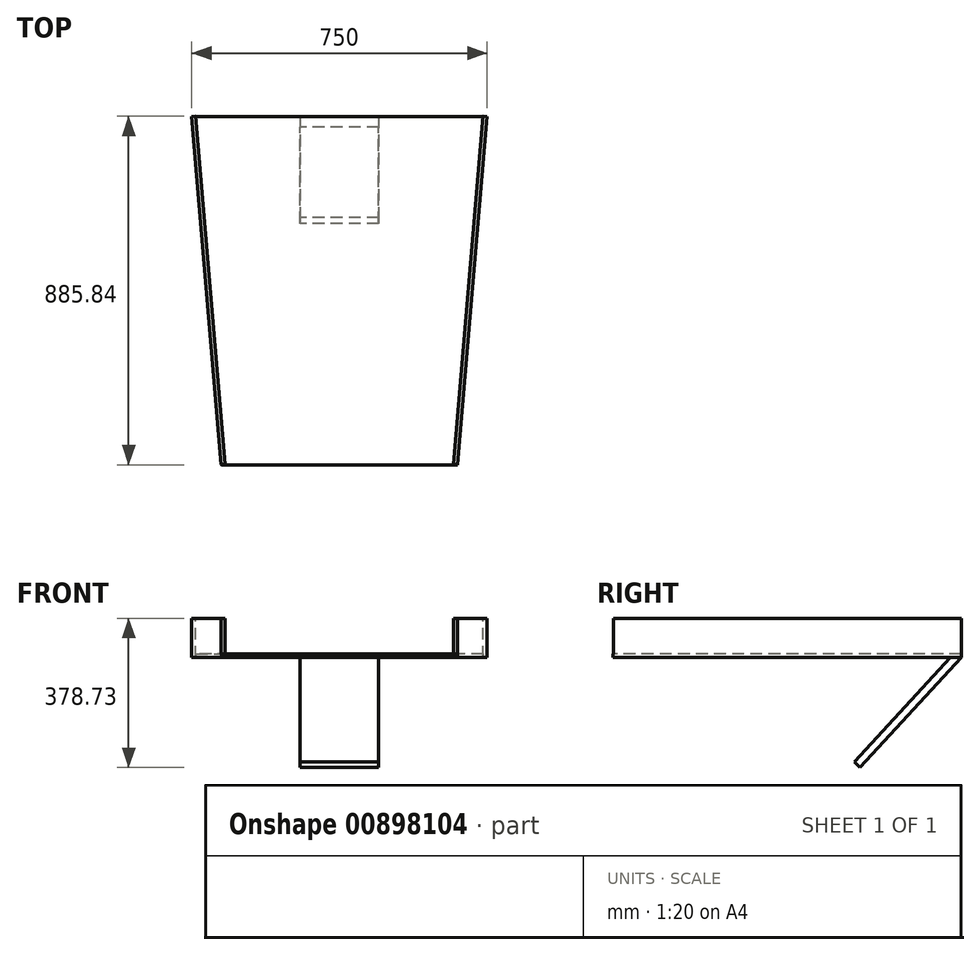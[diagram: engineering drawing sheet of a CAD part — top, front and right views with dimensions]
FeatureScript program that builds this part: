
annotation { "Feature Type Name" : "Feature", "Feature Type Description" : "" }
export const myFeature = defineFeature(function(context is Context, id is Id, definition is map)
    precondition{}
    {
        {
            var Q0;
            Q0=qCreatedBy(makeId("Top.planeOp"),FACE);
            var sketch = newSketch(context, id + "F0", { "sketchPlane" : qUnion([Q0])});
            skLineSegment(sketch, "E0.bottom", {"start": v(300, -442.5) * mm, "end": v(-300, -442.5) * mm});
            skLineSegment(sketch, "E0.top", {"start": v(375, 442.5) * mm, "end": v(-375, 442.5) * mm});
            skPoint(sketch, "E0.middle", {"position": v(0, 0) * mm});
            skLineSegment(sketch, "E1.bottom", {"start": v(-300, 442.5) * mm, "end": v(300, 442.5) * mm});
            skLineSegment(sketch, "E1.top", {"start": v(-300, -442.5) * mm, "end": v(300, -442.5) * mm});
            skLineSegment(sketch, "E2", {"start": v(-375, 442.5) * mm, "end": v(-300, -442.5) * mm});
            skLineSegment(sketch, "E3", {"start": v(300, -442.5) * mm, "end": v(375, 442.5) * mm});
            skPoint(sketch, "E4.orphan", {"position": v(-375, -442.5) * mm});
            skPoint(sketch, "E0.left.start.orphan", {"position": v(375, -442.5) * mm});
            skSolve(sketch);
        }
        {
            var Q0;
            {var subQ0=sQuery(id+"F0.wireOp",EDGE,"E1.bottom");Q0=makeQuery(id+"F0.imprint","IMPRINT",FACE,{"disambiguationData":[TD([[makeQuery(id+"F0.imprint","IMPRINT",EDGE,{"derivedFrom":subQ0}),-1.0]])]});}
            var Q1;
            Q1 = qSketchRegion(id + "F0", true);
            extrude(context, id + "F1", {"entities" : qUnion([Q0, Q1]), "depth" : 10 * mm, "offsetDistance" : 25 * mm});
        }
        {
            var Q0;
            Q0=makeQuery(id+"F1.opExtrude","SWEPT_FACE",FACE,{"disambiguationData":[OSD([sQuery(id+"F0.wireOp",EDGE,"E2")])]});
            var sketch = newSketch(context, id + "F2", { "sketchPlane" : qUnion([Q0])});
            skLineSegment(sketch, "E5.bottom", {"start": v(-472.59, 0) * mm, "end": v(414.67, 0) * mm});
            skLineSegment(sketch, "E5.top", {"start": v(-472.59, 100) * mm, "end": v(414.67, 100) * mm});
            skLineSegment(sketch, "E5.left", {"start": v(-472.59, 0) * mm, "end": v(-472.59, 100) * mm});
            skLineSegment(sketch, "E5.right", {"start": v(414.67, 0) * mm, "end": v(414.67, 100) * mm});
            skSolve(sketch);
        }
        {
            var Q0;
            Q0 = qSketchRegion(id + "F2", true);
            extrude(context, id + "F3", {"entities" : qUnion([Q0]), "operationType" : NewBodyOperationType.ADD, "oppositeDirection" : true, "depth" : 10 * mm, "offsetDistance" : 25 * mm});
        }
        {
            var Q0;
            Q0=makeQuery(id+"F1.opExtrude","SWEPT_BODY",BODY,{"disambiguationData":[OSD([sQuery(id+"F0.wireOp",EDGE,"E0.top"),sQuery(id+"F0.wireOp",EDGE,"E1.bottom"),sQuery(id+"F0.wireOp",EDGE,"E1.top"),sQuery(id+"F0.wireOp",EDGE,"E2"),sQuery(id+"F0.wireOp",EDGE,"E3")])]});
            var Q1;
            Q1=qCreatedBy(makeId("Right.planeOp"),FACE);
            mirror(context, id + "F4", {"operationType" : NewBodyOperationType.ADD, "entities" : qUnion([Q0]), "mirrorPlane" : qUnion([Q1])});
        }
        {
            var Q0;
            Q0=qCreatedBy(makeId("Right.planeOp"),FACE);
            var sketch = newSketch(context, id + "F5", { "sketchPlane" : qUnion([Q0])});
            skLineSegment(sketch, "E6.0", {"start": v(442.5, 0) * mm, "end": v(-442.5, 0) * mm});
            skLineSegment(sketch, "E7", {"start": v(442.5, 0) * mm, "end": v(185.3, -278.73) * mm});
            skLineSegment(sketch, "E8", {"start": v(170.6, -265.17) * mm, "end": v(415.29, 0) * mm});
            skLineSegment(sketch, "E9", {"start": v(185.3, -278.73) * mm, "end": v(170.6, -265.17) * mm});
            skSolve(sketch);
        }
        {
            var Q0;
            Q0 = qSketchRegion(id + "F5", true);
            extrude(context, id + "F6", {"entities" : qUnion([Q0]), "operationType" : NewBodyOperationType.ADD, "endBound" : BoundingType.SYMMETRIC, "depth" : 200 * mm, "offsetDistance" : 25 * mm});
        }
    });
